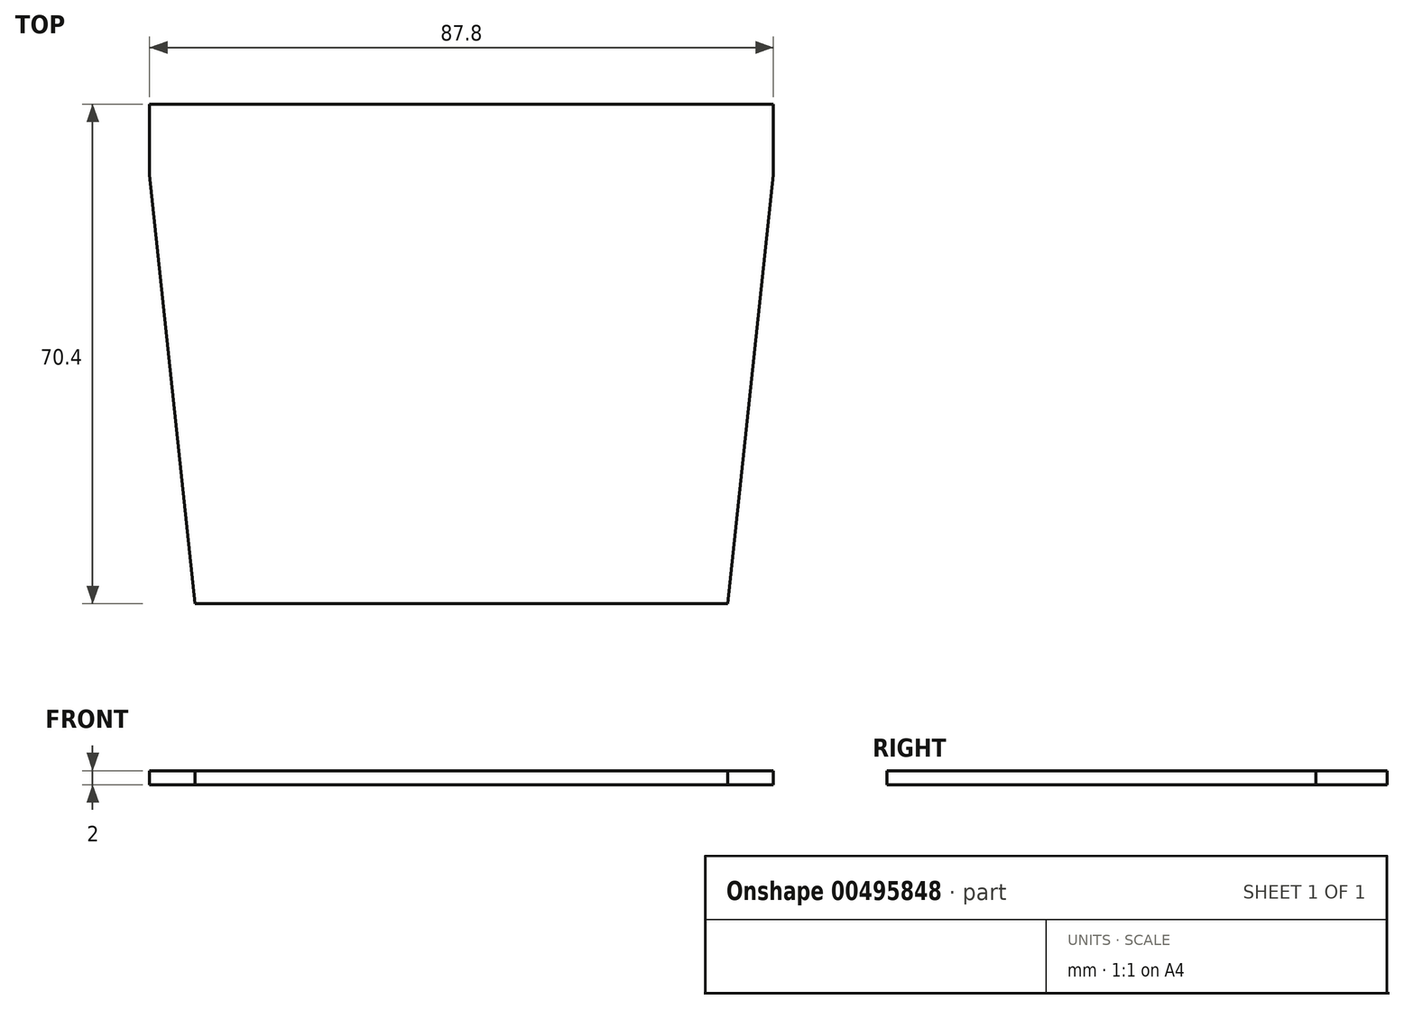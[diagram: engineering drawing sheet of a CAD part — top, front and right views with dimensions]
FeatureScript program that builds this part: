
annotation { "Feature Type Name" : "Feature", "Feature Type Description" : "" }
export const myFeature = defineFeature(function(context is Context, id is Id, definition is map)
    precondition{}
    {
        {
            var Q0;
            Q0=qCreatedBy(makeId("Top.planeOp"),FACE);
            var sketch = newSketch(context, id + "F0", { "sketchPlane" : qUnion([Q0])});
            skLineSegment(sketch, "E0", {"start": v(-43.9, 70.4) * mm, "end": v(43.9, 70.4) * mm});
            skLineSegment(sketch, "E1", {"start": v(43.9, 70.4) * mm, "end": v(43.9, 60.4) * mm});
            skLineSegment(sketch, "E2", {"start": v(43.9, 60.4) * mm, "end": v(37.5, 0) * mm});
            skLineSegment(sketch, "E3", {"start": v(37.5, 0) * mm, "end": v(-37.5, 0) * mm});
            skLineSegment(sketch, "E4", {"start": v(-37.5, 0) * mm, "end": v(-43.9, 60.4) * mm});
            skLineSegment(sketch, "E5", {"start": v(-43.9, 60.4) * mm, "end": v(-43.9, 70.4) * mm});
            skLineSegment(sketch, "E6", {"start": v(0, 0) * mm, "end": v(0, 98.6) * mm, "construction": true});
            skSolve(sketch);
        }
        {
            var Q0;
            Q0=qSketchRegion(id+"F0",true);
            extrude(context, id + "F1", {"entities" : qUnion([Q0]), "depth" : 2 * mm});
        }
    });
